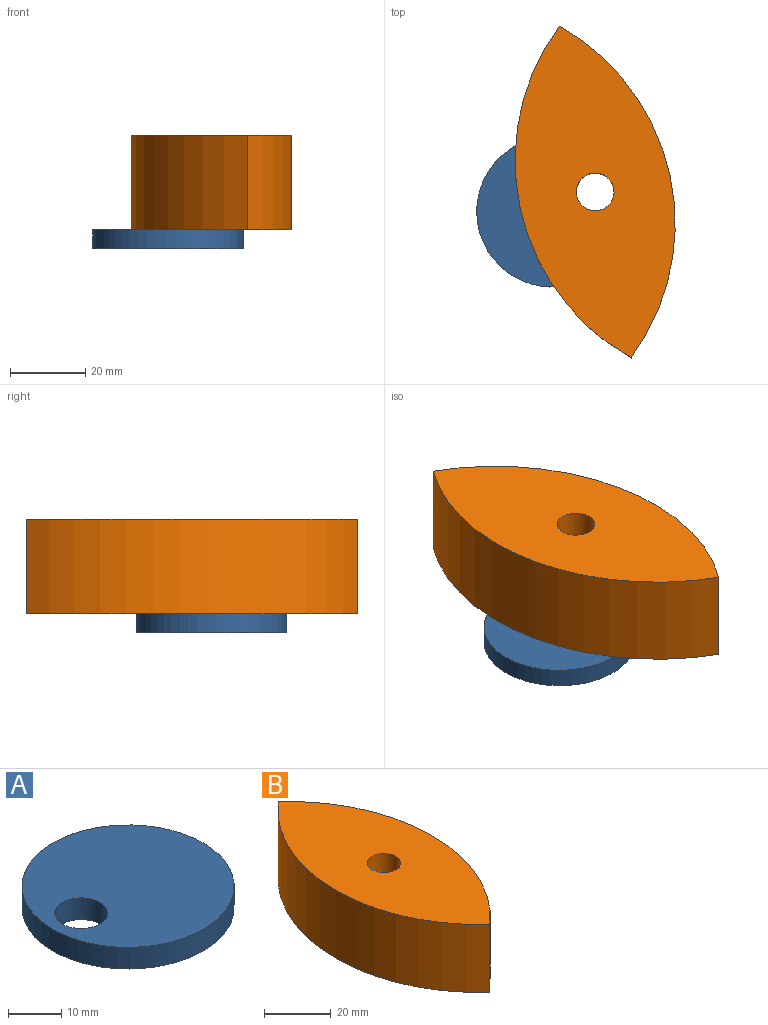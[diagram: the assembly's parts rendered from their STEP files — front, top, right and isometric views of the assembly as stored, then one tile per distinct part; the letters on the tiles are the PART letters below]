
ASSEMBLY  parts=2 mates=1
PART A: 4 faces, bbox 40x40x5 mm
  f0: cylinder r=5mm len=10mm, axis (0,0,1), area 157.1mm2, adj f2,f3
  f1: cylinder r=20mm len=40mm, axis (0,0,1), area 628.3mm2, adj f2,f3
  f2: plane 40x40mm, normal (0,0,-1), area 1178.1mm2, adj f0,f1
  f3: plane 40x40mm, normal (0,0,1), area 1178.1mm2, adj f0,f1
PART B: 5 faces, bbox 40.6x90x25 mm
  f0: cylinder r=60mm len=90mm, axis (0,0,-1), area 2544.2mm2, adj f1,f3,f4
  f1: cylinder r=60mm len=90mm, axis (0,0,-1), area 2544.2mm2, adj f0,f3,f4
  f2: cylinder r=5mm len=25mm, axis (0,0,-1), area 785.4mm2, adj f3,f4
  f3: plane 90x40.63mm, normal (0,0,1), area 2455.7mm2, adj f0,f1,f2
  f4: plane 90x40.63mm, normal (0,0,-1), area 2455.7mm2, adj f0,f1,f2
PLACE A rot(axis=(0,0,-1),155.6deg) t=(-11.38,-5.17,0)mm
PLACE B rot(axis=(0,0,1),12.2deg) t=(35.81,10.46,0)mm
MATE revolute A.f0 <-> B.f2  axis (0,0,1) through (11.38,5.17,0)mm
